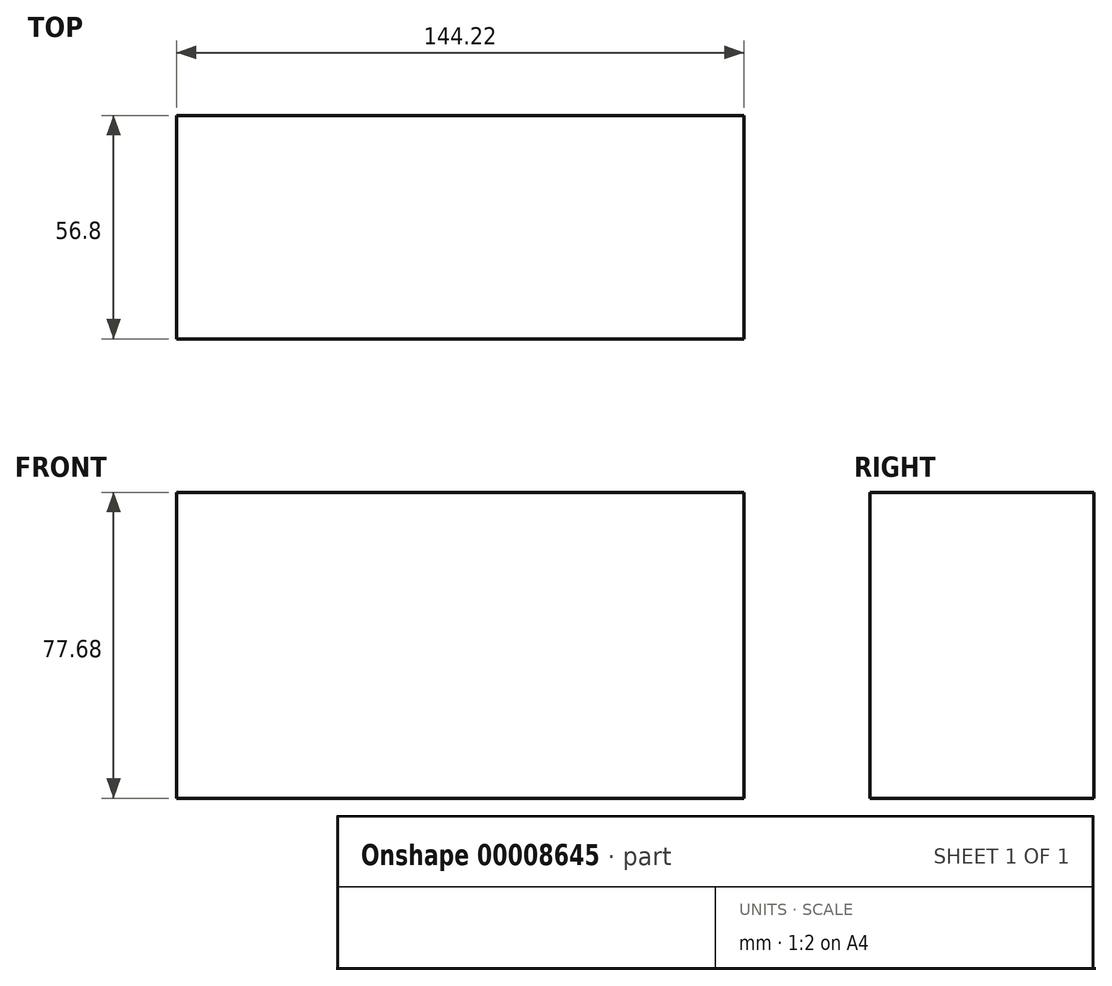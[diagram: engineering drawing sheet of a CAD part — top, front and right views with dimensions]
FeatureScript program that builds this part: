
annotation { "Feature Type Name" : "Feature", "Feature Type Description" : "" }
export const myFeature = defineFeature(function(context is Context, id is Id, definition is map)
    precondition{}
    {
        {
            var Q0;
            Q0=qCreatedBy(makeId("Top.planeOp"),FACE);
            var sketch = newSketch(context, id + "F0", { "sketchPlane" : qUnion([Q0])});
            skLineSegment(sketch, "E0.bottom", {"start": v(0, 0) * mm, "end": v(-144.22, 0) * mm});
            skLineSegment(sketch, "E0.top", {"start": v(0, 56.8) * mm, "end": v(-144.22, 56.8) * mm});
            skLineSegment(sketch, "E0.left", {"start": v(0, 0) * mm, "end": v(0, 56.8) * mm});
            skLineSegment(sketch, "E0.right", {"start": v(-144.22, 0) * mm, "end": v(-144.22, 56.8) * mm});
            skSolve(sketch);
        }
        {
            var Q0;
            Q0=makeQuery(id+"F0.imprint","IMPRINT",FACE,{"disambiguationData":[TD([[makeQuery(id+"F0.imprint","IMPRINT",EDGE,{"derivedFrom":sQuery(id+"F0.wireOp",EDGE,"E0.bottom")}),-1.0]])]});
            extrude(context, id + "F1", {"entities" : qUnion([Q0]), "depth" : 77.68 * mm});
        }
    });
